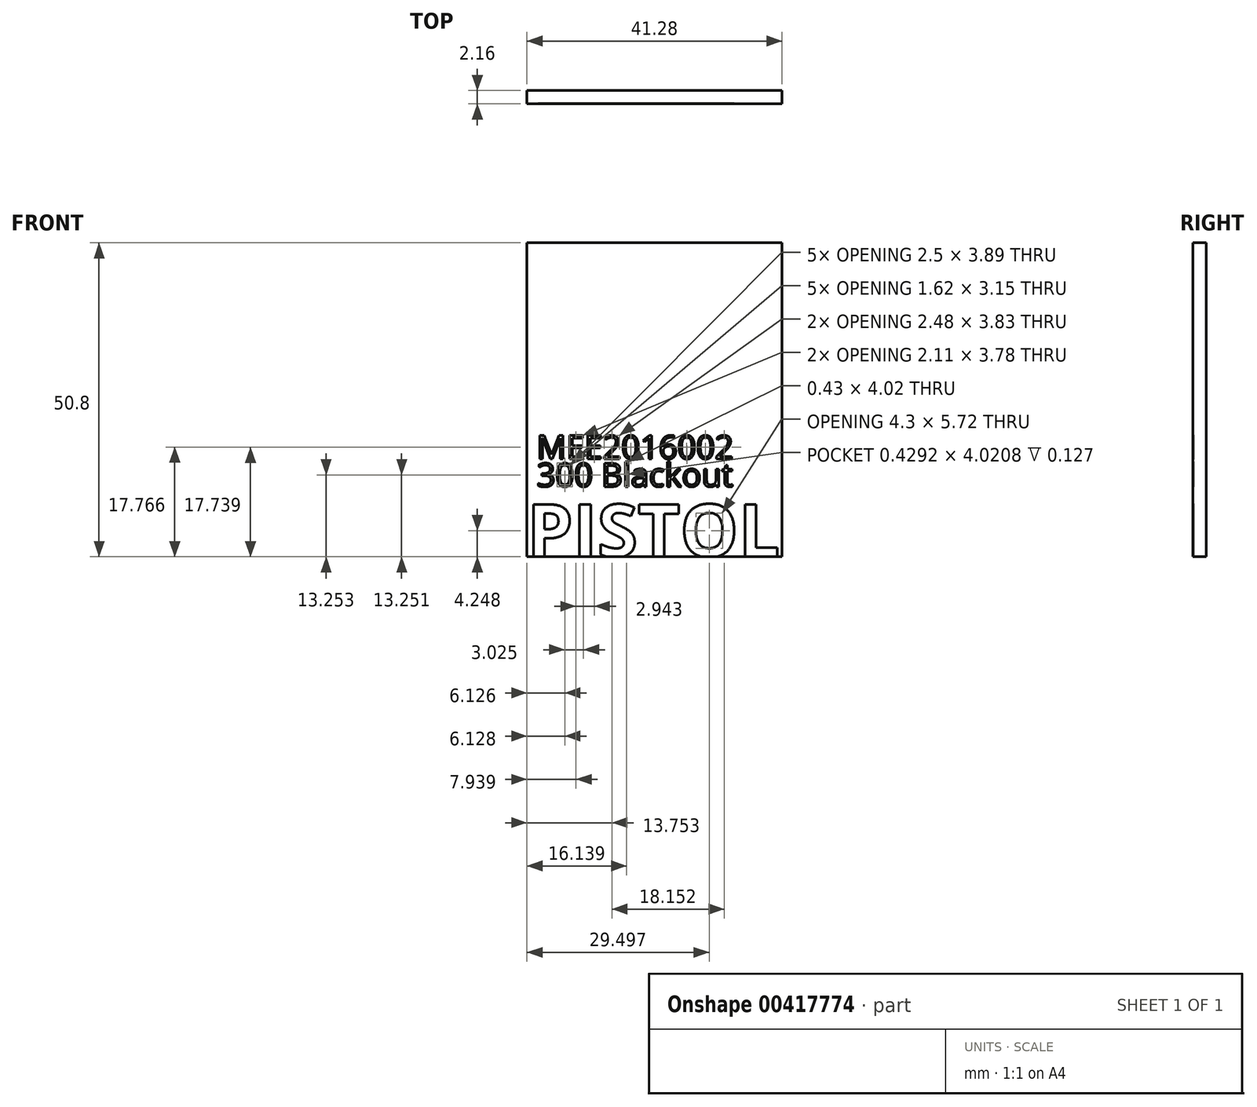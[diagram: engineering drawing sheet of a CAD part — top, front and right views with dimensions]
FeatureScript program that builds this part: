
annotation { "Feature Type Name" : "Feature", "Feature Type Description" : "" }
export const myFeature = defineFeature(function(context is Context, id is Id, definition is map)
    precondition{}
    {
        {
            var Q0;
            Q0=qCreatedBy(makeId("Front.planeOp"),FACE);
            var sketch = newSketch(context, id + "F0", { "sketchPlane" : qUnion([Q0])});
            skLineSegment(sketch, "E0.bottom", {"start": v(0, 50.8) * mm, "end": v(41.28, 50.8) * mm});
            skLineSegment(sketch, "E0.top", {"start": v(0, 0) * mm, "end": v(41.28, 0) * mm});
            skLineSegment(sketch, "E0.left", {"start": v(0, 50.8) * mm, "end": v(0, 0) * mm});
            skLineSegment(sketch, "E0.right", {"start": v(41.28, 50.8) * mm, "end": v(41.28, 0) * mm});
            skSolve(sketch);
        }
        {
            var Q0;
            Q0 = qSketchRegion(id + "F0", true);
            extrude(context, id + "F1", {"entities" : qUnion([Q0]), "oppositeDirection" : true, "depth" : 2.16 * mm});
        }
        {
            var Q0;
            Q0=makeQuery(id+"F1.opExtrude","CAP_FACE",FACE,{"disambiguationData":[OSD([sQuery(id+"F0.wireOp",EDGE,"E0.bottom"),sQuery(id+"F0.wireOp",EDGE,"E0.top"),sQuery(id+"F0.wireOp",EDGE,"E0.left"),sQuery(id+"F0.wireOp",EDGE,"E0.right")])],"isStart":true});
            var sketch = newSketch(context, id + "F2", { "sketchPlane" : qUnion([Q0])});
            skText(sketch, "E1", { "text": "PISTOL", "fontName": "OpenSans-Bold.ttf"});
            const initialGuessF2  = {"E1": [0, 0, 1, 0, 0.00854]};
            skSetInitialGuess(sketch, initialGuessF2);
            skSolve(sketch);
        }
        {
            var Q0;
            Q0 = qSketchRegion(id + "F2", true);
            extrude(context, id + "F3", {"entities" : qUnion([Q0]), "operationType" : NewBodyOperationType.REMOVE, "oppositeDirection" : true, "depth" : 0.13 * mm});
        }
        {
            var Q0;
            Q0=qCreatedBy(makeId("Front.planeOp"),FACE);
            var sketch = newSketch(context, id + "F4", { "sketchPlane" : qUnion([Q0])});
            skText(sketch, "E2", { "text": "MEE2016002\n\n", "fontName": "OpenSans-Regular.ttf"});
            const initialGuessF4  = {"E2": [0.00159, 0.01585, 1, 0, 0.00381]};
            skSetInitialGuess(sketch, initialGuessF4);
            skSolve(sketch);
        }
        {
            var Q0;
            Q0 = qSketchRegion(id + "F4", true);
            extrude(context, id + "F5", {"entities" : qUnion([Q0]), "operationType" : NewBodyOperationType.REMOVE, "oppositeDirection" : true, "depth" : 0.13 * mm});
        }
        {
            var Q0;
            {var subQ26=sQuery(id+"F0.wireOp",EDGE,"E0.left");var subQ30=sQuery(id+"F0.wireOp",EDGE,"E0.top");var subQ34=sQuery(id+"F0.wireOp",EDGE,"E0.right");var subQ42=sQuery(id+"F0.wireOp",EDGE,"E0.bottom");var subQ43=makeQuery(id+"F1.opExtrude","SWEPT_FACE",FACE,{"disambiguationData":[OSD([subQ42])]});Q0=makeQuery(id+"F5.boolean.opBoolean","SPLIT",FACE,{"disambiguationData":[TD([subQ43])],"derivedFrom":makeQuery(id+"F3.boolean.opBoolean","SPLIT",FACE,{"disambiguationData":[TD([subQ43])],"derivedFrom":makeQuery(id+"F1.opExtrude","CAP_FACE",FACE,{"disambiguationData":[OSD([subQ42,subQ30,subQ26,subQ34])],"isStart":true})})});}
            var sketch = newSketch(context, id + "F6", { "sketchPlane" : qUnion([Q0])});
            skText(sketch, "E3", { "text": "300 Blackout\n", "fontName": "OpenSans-Regular.ttf"});
            const initialGuessF6  = {"E3": [0.00159, 0.01136, 1, 0, 0.00381]};
            skSetInitialGuess(sketch, initialGuessF6);
            skSolve(sketch);
        }
        {
            var Q0;
            Q0 = qSketchRegion(id + "F6", true);
            extrude(context, id + "F7", {"entities" : qUnion([Q0]), "operationType" : NewBodyOperationType.REMOVE, "oppositeDirection" : true, "depth" : 0.13 * mm});
        }
    });
